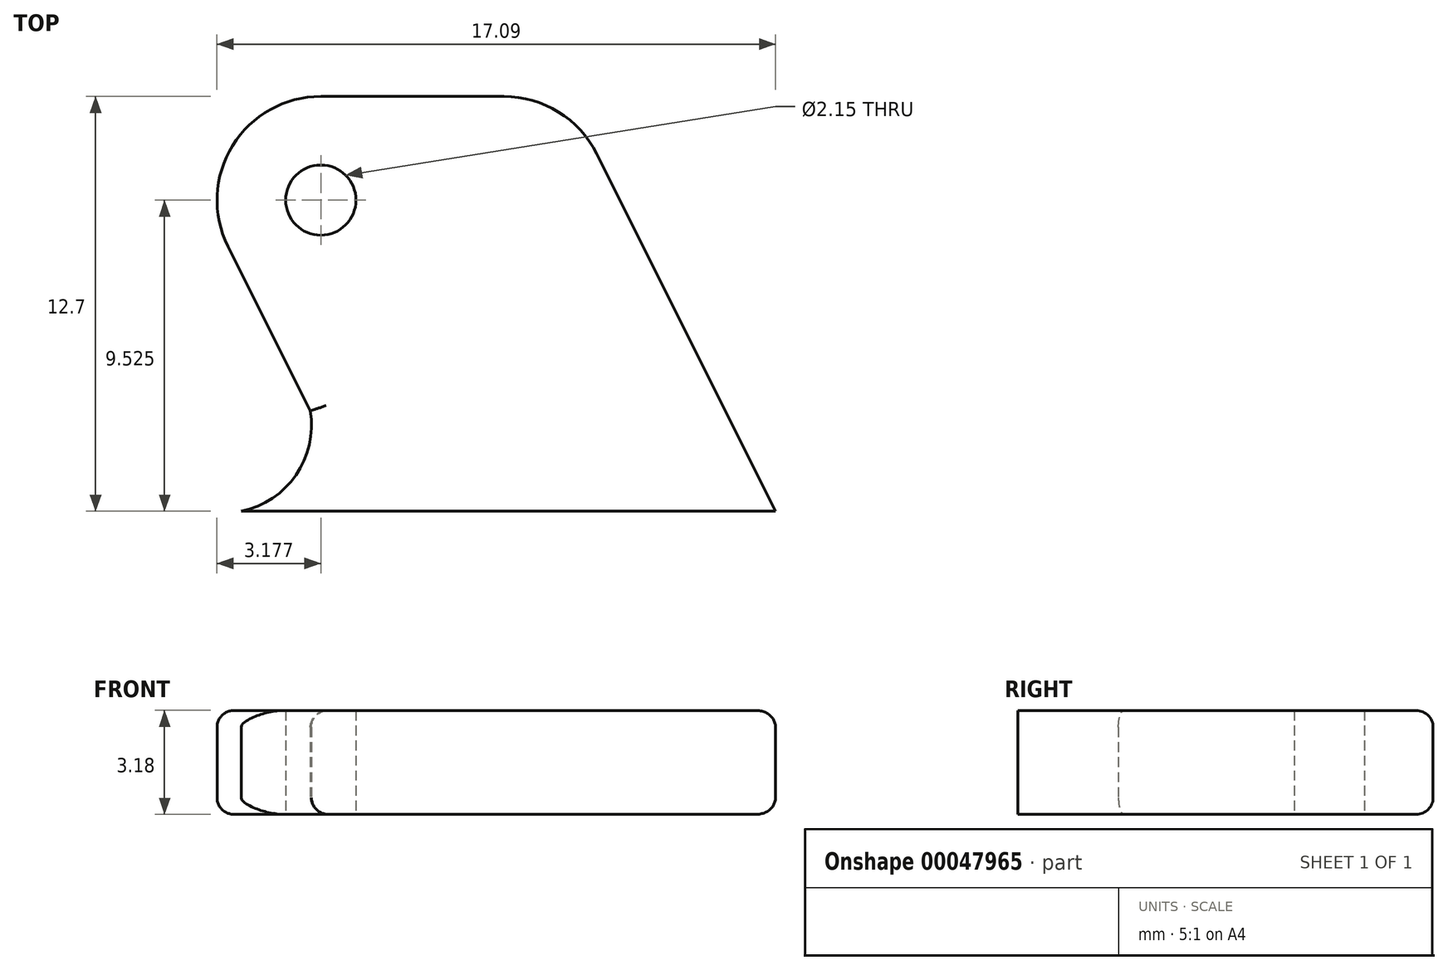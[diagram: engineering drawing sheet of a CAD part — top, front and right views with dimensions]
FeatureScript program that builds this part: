
annotation { "Feature Type Name" : "Feature", "Feature Type Description" : "" }
export const myFeature = defineFeature(function(context is Context, id is Id, definition is map)
    precondition{}
    {
        {
            var Q0;
            Q0=qCreatedBy(makeId("Top.planeOp"),FACE);
            var sketch = newSketch(context, id + "F0", { "sketchPlane" : qUnion([Q0])});
            skLineSegment(sketch, "E0", {"start": v(0, 0) * mm, "end": v(-12.7, 0) * mm});
            skLineSegment(sketch, "E1", {"start": v(0, 0) * mm, "end": v(-5.47, 10.94) * mm});
            skLineSegment(sketch, "E2", {"start": v(-16.75, 8.1) * mm, "end": v(-14.24, 3.07) * mm});
            skLineSegment(sketch, "E3", {"start": v(-13.91, 12.7) * mm, "end": v(-8.31, 12.7) * mm});
            skPoint(sketch, "E4.visualSharp", {"position": v(-19.05, 12.7) * mm});
            skArc(sketch, "E4.filletArc", {"start": v(-13.91, 12.7) * mm, "mid": v(-16.61, 11.2) * mm, "end": v(-16.75, 8.1) * mm});
            skPoint(sketch, "E5.visualSharp", {"position": v(-6.35, 12.7) * mm});
            skArc(sketch, "E5.filletArc", {"start": v(-5.47, 10.94) * mm, "mid": v(-6.64, 12.23) * mm, "end": v(-8.31, 12.7) * mm});
            skArc(sketch, "E6", {"start": v(-16.35, 0) * mm, "mid": v(-14.67, 1.1) * mm, "end": v(-14.24, 3.07) * mm});
            skLineSegment(sketch, "E7", {"start": v(-16.35, 0) * mm, "end": v(-12.7, 0) * mm});
            skCircle(sketch, "E8", {"center": v(-13.91, 9.52) * mm, "radius": 1.07 * mm});
            skSolve(sketch);
        }
        {
            var Q0;
            Q0=makeQuery(id+"F0.imprint","IMPRINT",FACE,{"disambiguationData":[TD([[makeQuery(id+"F0.imprint","IMPRINT",EDGE,{"derivedFrom":sQuery(id+"F0.wireOp",EDGE,"E0")}),-1.0]])]});
            extrude(context, id + "F1", {"entities" : qUnion([Q0]), "depth" : 3.17 * mm});
        }
        {
            var Q0;
            Q0=makeQuery(id+"F1.opExtrude","CAP_EDGE",EDGE,{"disambiguationData":[OSD([sQuery(id+"F0.wireOp",EDGE,"E1")])],"isStart":true});
            var Q1;
            Q1=makeQuery(id+"F1.opExtrude","CAP_EDGE",EDGE,{"disambiguationData":[OSD([sQuery(id+"F0.wireOp",EDGE,"E5.filletArc")])],"isStart":true});
            var Q2;
            Q2=makeQuery(id+"F1.opExtrude","CAP_EDGE",EDGE,{"disambiguationData":[OSD([sQuery(id+"F0.wireOp",EDGE,"E3")])],"isStart":true});
            var Q3;
            Q3=makeQuery(id+"F1.opExtrude","CAP_EDGE",EDGE,{"disambiguationData":[OSD([sQuery(id+"F0.wireOp",EDGE,"E4.filletArc")])],"isStart":true});
            var Q4;
            Q4=makeQuery(id+"F1.opExtrude","CAP_EDGE",EDGE,{"disambiguationData":[OSD([sQuery(id+"F0.wireOp",EDGE,"E2")])],"isStart":true});
            var Q5;
            Q5=makeQuery(id+"F1.opExtrude","CAP_EDGE",EDGE,{"disambiguationData":[OSD([sQuery(id+"F0.wireOp",EDGE,"E6")])],"isStart":true});
            var Q6;
            Q6=makeQuery(id+"F1.opExtrude","CAP_EDGE",EDGE,{"disambiguationData":[OSD([sQuery(id+"F0.wireOp",EDGE,"E1")])],"isStart":false});
            var Q7;
            Q7=makeQuery(id+"F1.opExtrude","CAP_EDGE",EDGE,{"disambiguationData":[OSD([sQuery(id+"F0.wireOp",EDGE,"E5.filletArc")])],"isStart":false});
            var Q8;
            Q8=makeQuery(id+"F1.opExtrude","CAP_EDGE",EDGE,{"disambiguationData":[OSD([sQuery(id+"F0.wireOp",EDGE,"E3")])],"isStart":false});
            var Q9;
            Q9=makeQuery(id+"F1.opExtrude","CAP_EDGE",EDGE,{"disambiguationData":[OSD([sQuery(id+"F0.wireOp",EDGE,"E4.filletArc")])],"isStart":false});
            var Q10;
            Q10=makeQuery(id+"F1.opExtrude","CAP_EDGE",EDGE,{"disambiguationData":[OSD([sQuery(id+"F0.wireOp",EDGE,"E2")])],"isStart":false});
            var Q11;
            Q11=makeQuery(id+"F1.opExtrude","CAP_EDGE",EDGE,{"disambiguationData":[OSD([sQuery(id+"F0.wireOp",EDGE,"E6")])],"isStart":false});
            fillet(context, id + "F2", {"entities" : qUnion([Q0, Q1, Q2, Q3, Q4, Q5, Q6, Q7, Q8, Q9, Q10, Q11]), "radius" : 0.5 * mm, "tangentPropagation" : true, "allowEdgeOverflow" : false});
        }
    });
